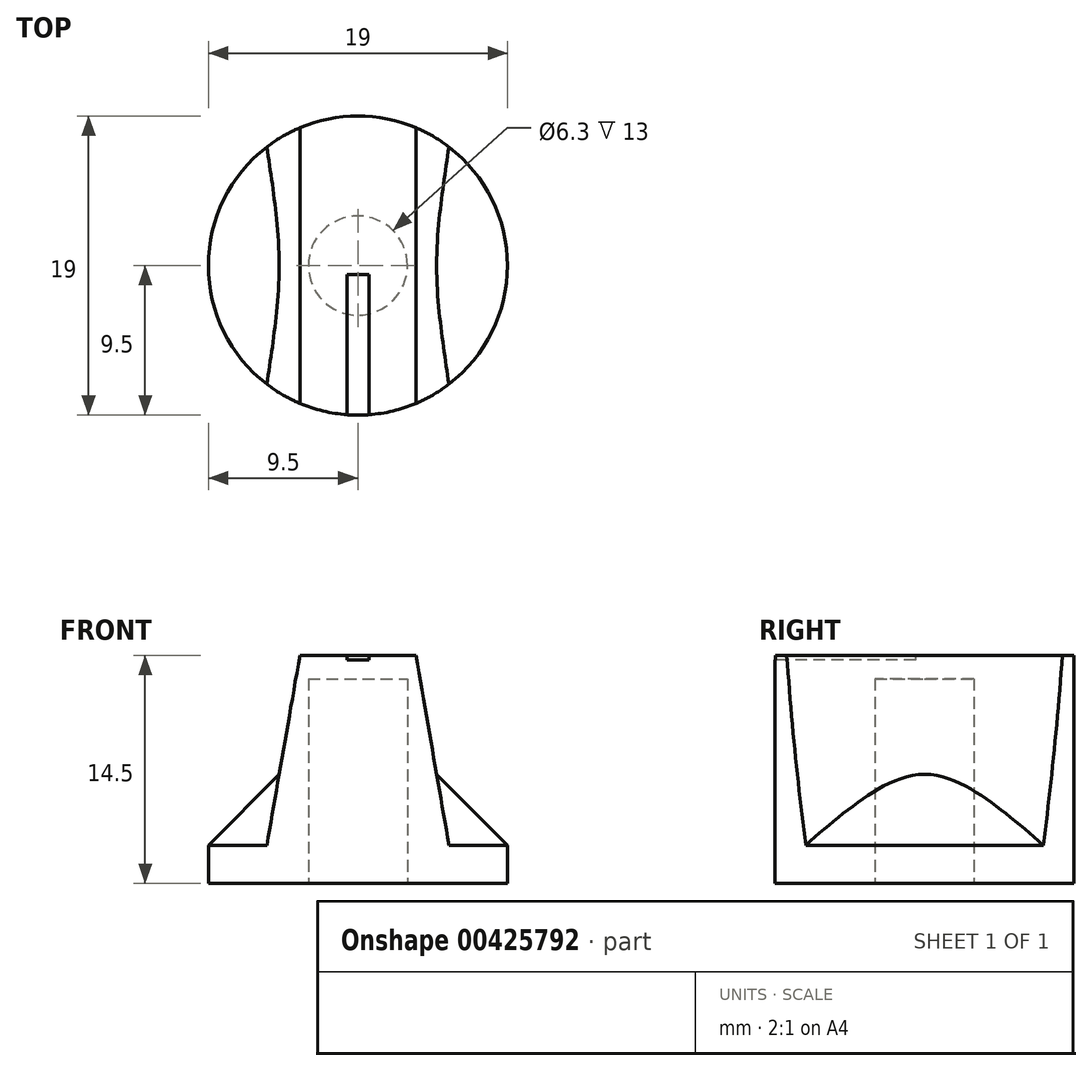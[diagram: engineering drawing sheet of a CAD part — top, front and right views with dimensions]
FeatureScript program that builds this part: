
annotation { "Feature Type Name" : "Feature", "Feature Type Description" : "" }
export const myFeature = defineFeature(function(context is Context, id is Id, definition is map)
    precondition{}
    {
        {
            var Q0;
            Q0=qCreatedBy(makeId("Top.planeOp"),FACE);
            var sketch = newSketch(context, id + "F0", { "sketchPlane" : qUnion([Q0])});
            skCircle(sketch, "E0", {"center": v(0, 0) * mm, "radius": 9.5 * mm});
            skSolve(sketch);
        }
        {
            var Q0;
            Q0 = qSketchRegion(id + "F0", true);
            extrude(context, id + "F1", {"entities" : qUnion([Q0]), "depth" : 14.5 * mm});
        }
        {
            var Q0;
            Q0=makeQuery(id+"F1.opExtrude","CAP_FACE",FACE,{"disambiguationData":[OSD([sQuery(id+"F0.wireOp",EDGE,"E0")])],"isStart":true});
            var sketch = newSketch(context, id + "F2", { "sketchPlane" : qUnion([Q0])});
            skCircle(sketch, "E1", {"center": v(0, 0) * mm, "radius": 3.15 * mm});
            skSolve(sketch);
        }
        {
            var Q0;
            Q0 = qSketchRegion(id + "F2", true);
            extrude(context, id + "F3", {"entities" : qUnion([Q0]), "operationType" : NewBodyOperationType.REMOVE, "oppositeDirection" : true, "depth" : 13 * mm});
        }
        {
            var Q0;
            Q0=qCreatedBy(makeId("Front.planeOp"),FACE);
            var sketch = newSketch(context, id + "F4", { "sketchPlane" : qUnion([Q0])});
            skLineSegment(sketch, "E2", {"start": v(3.68, 14.5) * mm, "end": v(5, 6.94) * mm});
            skLineSegment(sketch, "E3", {"start": v(5, 6.94) * mm, "end": v(9.72, 6.94) * mm});
            skLineSegment(sketch, "E4", {"start": v(0, 15.68) * mm, "end": v(0, -2.4) * mm, "construction": true});
            skLineSegment(sketch, "E5.MirrorCS", {"start": v(-3.68, 14.5) * mm, "end": v(-5, 6.94) * mm});
            skLineSegment(sketch, "E6.MirrorCS", {"start": v(-5, 6.94) * mm, "end": v(-9.72, 6.94) * mm});
            skLineSegment(sketch, "E7", {"start": v(3.68, 14.5) * mm, "end": v(5, 16.33) * mm});
            skLineSegment(sketch, "E8", {"start": v(5, 16.33) * mm, "end": v(12.48, 14.99) * mm});
            skLineSegment(sketch, "E9", {"start": v(12.48, 14.99) * mm, "end": v(9.72, 6.94) * mm});
            skLineSegment(sketch, "E10.MirrorCS", {"start": v(-3.68, 14.5) * mm, "end": v(-5, 16.33) * mm});
            skLineSegment(sketch, "E11.MirrorCS", {"start": v(-5, 16.33) * mm, "end": v(-12.48, 14.99) * mm});
            skLineSegment(sketch, "E12.MirrorCS", {"start": v(-12.48, 14.99) * mm, "end": v(-9.72, 6.94) * mm});
            skSolve(sketch);
        }
        {
            var Q0;
            Q0 = qSketchRegion(id + "F4", true);
            extrude(context, id + "F5", {"entities" : qUnion([Q0]), "operationType" : NewBodyOperationType.REMOVE, "endBound" : BoundingType.SYMMETRIC, "oppositeDirection" : true, "depth" : 25 * mm});
        }
        {
            var Q0;
            Q0=makeQuery(id+"F5.boolean.opBoolean","INTERSECT",EDGE,{"derivedFrom":[makeQuery(id+"F1.opExtrude","SWEPT_FACE",FACE,{"disambiguationData":[OSD([sQuery(id+"F0.wireOp",EDGE,"E0")])]}),makeQuery(id+"F5.opExtrude","SWEPT_FACE",FACE,{"disambiguationData":[OSD([sQuery(id+"F4.wireOp",EDGE,"E3")])]})]});
            var Q1;
            Q1=makeQuery(id+"F5.boolean.opBoolean","INTERSECT",EDGE,{"derivedFrom":[makeQuery(id+"F1.opExtrude","SWEPT_FACE",FACE,{"disambiguationData":[OSD([sQuery(id+"F0.wireOp",EDGE,"E0")])]}),makeQuery(id+"F5.opExtrude","SWEPT_FACE",FACE,{"disambiguationData":[OSD([sQuery(id+"F4.wireOp",EDGE,"E6.MirrorCS")])]})]});
            chamfer(context, id + "F6", {"entities" : qUnion([Q0, Q1]), "width" : 4.5 * mm, "tangentPropagation" : true});
        }
        {
            var Q0;
            Q0=makeQuery(id+"F1.opExtrude","CAP_FACE",FACE,{"disambiguationData":[OSD([sQuery(id+"F0.wireOp",EDGE,"E0")])],"isStart":false});
            var sketch = newSketch(context, id + "F7", { "sketchPlane" : qUnion([Q0])});
            skLineSegment(sketch, "E13.bottom", {"start": v(-0.7, -0.56) * mm, "end": v(0.7, -0.56) * mm});
            skLineSegment(sketch, "E13.top", {"start": v(-0.7, -9.84) * mm, "end": v(0.7, -9.84) * mm});
            skLineSegment(sketch, "E13.left", {"start": v(-0.7, -0.56) * mm, "end": v(-0.7, -9.84) * mm});
            skLineSegment(sketch, "E13.right", {"start": v(0.7, -0.56) * mm, "end": v(0.7, -9.84) * mm});
            skSolve(sketch);
        }
        {
            var Q0;
            Q0 = qSketchRegion(id + "F7", true);
            extrude(context, id + "F8", {"entities" : qUnion([Q0]), "operationType" : NewBodyOperationType.REMOVE, "oppositeDirection" : true, "depth" : 0.3 * mm});
        }
    });
